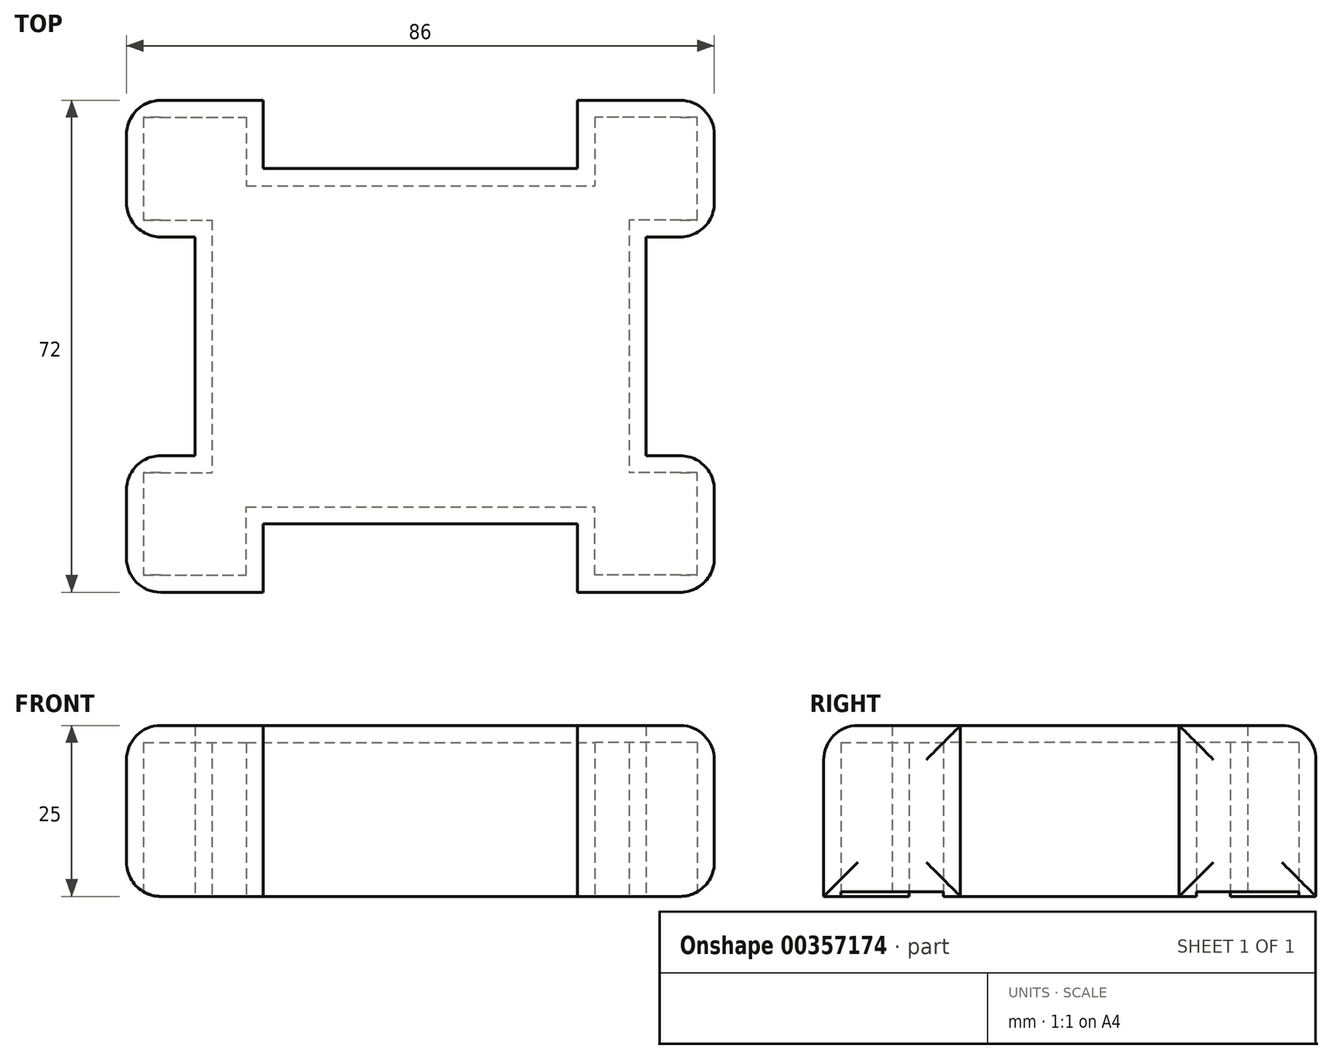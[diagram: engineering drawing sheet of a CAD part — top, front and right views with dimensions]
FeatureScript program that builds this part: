
annotation { "Feature Type Name" : "Feature", "Feature Type Description" : "" }
export const myFeature = defineFeature(function(context is Context, id is Id, definition is map)
    precondition{}
    {
        {
            var Q0;
            Q0=qCreatedBy(makeId("Top.planeOp"),FACE);
            var sketch = newSketch(context, id + "F0", { "sketchPlane" : qUnion([Q0])});
            skLineSegment(sketch, "E0.bottom", {"start": v(-33, 26) * mm, "end": v(33, 26) * mm});
            skLineSegment(sketch, "E0.top", {"start": v(-33, -26) * mm, "end": v(33, -26) * mm});
            skLineSegment(sketch, "E0.left", {"start": v(-33, 26) * mm, "end": v(-33, -26) * mm});
            skLineSegment(sketch, "E0.right", {"start": v(33, 26) * mm, "end": v(33, -26) * mm});
            skPoint(sketch, "E0.middle", {"position": v(0, 0) * mm});
            skLineSegment(sketch, "E1.bottom", {"start": v(-43, -36) * mm, "end": v(-23, -36) * mm});
            skLineSegment(sketch, "E1.top", {"start": v(-43, -16) * mm, "end": v(-23, -16) * mm});
            skLineSegment(sketch, "E1.left", {"start": v(-43, -36) * mm, "end": v(-43, -16) * mm});
            skLineSegment(sketch, "E1.right", {"start": v(-23, -36) * mm, "end": v(-23, -16) * mm});
            skPoint(sketch, "E1.middle", {"position": v(-33, -26) * mm});
            skLineSegment(sketch, "E2.bottom", {"start": v(43, -36) * mm, "end": v(23, -36) * mm});
            skLineSegment(sketch, "E2.top", {"start": v(43, -16) * mm, "end": v(23, -16) * mm});
            skLineSegment(sketch, "E2.left", {"start": v(43, -36) * mm, "end": v(43, -16) * mm});
            skLineSegment(sketch, "E2.right", {"start": v(23, -36) * mm, "end": v(23, -16) * mm});
            skPoint(sketch, "E2.middle", {"position": v(33, -26) * mm});
            skLineSegment(sketch, "E3.bottom", {"start": v(43, 36) * mm, "end": v(23, 36) * mm});
            skLineSegment(sketch, "E3.top", {"start": v(43, 16) * mm, "end": v(23, 16) * mm});
            skLineSegment(sketch, "E3.left", {"start": v(43, 36) * mm, "end": v(43, 16) * mm});
            skLineSegment(sketch, "E3.right", {"start": v(23, 36) * mm, "end": v(23, 16) * mm});
            skPoint(sketch, "E3.middle", {"position": v(33, 26) * mm});
            skLineSegment(sketch, "E4.bottom", {"start": v(-43, 36) * mm, "end": v(-23, 36) * mm});
            skLineSegment(sketch, "E4.top", {"start": v(-43, 16) * mm, "end": v(-23, 16) * mm});
            skLineSegment(sketch, "E4.left", {"start": v(-43, 36) * mm, "end": v(-43, 16) * mm});
            skLineSegment(sketch, "E4.right", {"start": v(-23, 36) * mm, "end": v(-23, 16) * mm});
            skPoint(sketch, "E4.middle", {"position": v(-33, 26) * mm});
            skSolve(sketch);
        }
        {
            var Q0;
            Q0 = qSketchRegion(id + "F0", true);
            extrude(context, id + "F1", {"entities" : qUnion([Q0]), "depth" : 25 * mm});
        }
        {
            var Q0;
            Q0=makeQuery(id+"F1.opExtrude","CAP_FACE",FACE,{"disambiguationData":[OSD([sQuery(id+"F0.wireOp",EDGE,"E0.bottom"),sQuery(id+"F0.wireOp",EDGE,"E0.top"),sQuery(id+"F0.wireOp",EDGE,"E0.left"),sQuery(id+"F0.wireOp",EDGE,"E0.right"),sQuery(id+"F0.wireOp",EDGE,"E1.bottom"),sQuery(id+"F0.wireOp",EDGE,"E1.top"),sQuery(id+"F0.wireOp",EDGE,"E1.left"),sQuery(id+"F0.wireOp",EDGE,"E1.right"),sQuery(id+"F0.wireOp",EDGE,"E2.bottom"),sQuery(id+"F0.wireOp",EDGE,"E2.top"),sQuery(id+"F0.wireOp",EDGE,"E2.left"),sQuery(id+"F0.wireOp",EDGE,"E2.right"),sQuery(id+"F0.wireOp",EDGE,"E3.bottom"),sQuery(id+"F0.wireOp",EDGE,"E3.top"),sQuery(id+"F0.wireOp",EDGE,"E3.left"),sQuery(id+"F0.wireOp",EDGE,"E3.right"),sQuery(id+"F0.wireOp",EDGE,"E4.bottom"),sQuery(id+"F0.wireOp",EDGE,"E4.top"),sQuery(id+"F0.wireOp",EDGE,"E4.left"),sQuery(id+"F0.wireOp",EDGE,"E4.right")])],"isStart":true});
            shell(context, id + "F2", {"entities" : qUnion([Q0]), "thickness" : 2.5 * mm});
        }
        {
            var Q0;
            Q0=makeQuery(id+"F1.opExtrude","CAP_EDGE",EDGE,{"disambiguationData":[OSD([sQuery(id+"F0.wireOp",EDGE,"E4.bottom")])],"isStart":false});
            var Q1;
            Q1=makeQuery(id+"F1.opExtrude","CAP_EDGE",EDGE,{"disambiguationData":[OSD([sQuery(id+"F0.wireOp",EDGE,"E1.bottom")])],"isStart":false});
            var Q2;
            Q2=makeQuery(id+"F1.opExtrude","CAP_EDGE",EDGE,{"disambiguationData":[OSD([sQuery(id+"F0.wireOp",EDGE,"E2.bottom")])],"isStart":false});
            var Q3;
            Q3=makeQuery(id+"F1.opExtrude","CAP_EDGE",EDGE,{"disambiguationData":[OSD([sQuery(id+"F0.wireOp",EDGE,"E3.bottom")])],"isStart":false});
            var Q4;
            Q4=makeQuery(id+"F1.opExtrude","CAP_EDGE",EDGE,{"disambiguationData":[OSD([sQuery(id+"F0.wireOp",EDGE,"E3.left")])],"isStart":false});
            var Q5;
            Q5=makeQuery(id+"F1.opExtrude","CAP_EDGE",EDGE,{"disambiguationData":[OSD([sQuery(id+"F0.wireOp",EDGE,"E2.left")])],"isStart":false});
            var Q6;
            Q6=makeQuery(id+"F1.opExtrude","CAP_EDGE",EDGE,{"disambiguationData":[OSD([sQuery(id+"F0.wireOp",EDGE,"E1.left")])],"isStart":false});
            var Q7;
            Q7=makeQuery(id+"F1.opExtrude","SWEPT_FACE",FACE,{"disambiguationData":[OSD([sQuery(id+"F0.wireOp",EDGE,"E4.left")])]});
            var Q8;
            Q8=makeQuery(id+"F1.opExtrude","SWEPT_FACE",FACE,{"disambiguationData":[OSD([sQuery(id+"F0.wireOp",EDGE,"E3.left")])]});
            var Q9;
            Q9=makeQuery(id+"F1.opExtrude","SWEPT_FACE",FACE,{"disambiguationData":[OSD([sQuery(id+"F0.wireOp",EDGE,"E2.left")])]});
            var Q10;
            Q10=makeQuery(id+"F1.opExtrude","SWEPT_FACE",FACE,{"disambiguationData":[OSD([sQuery(id+"F0.wireOp",EDGE,"E1.left")])]});
            fillet(context, id + "F3", {"entities" : qUnion([Q0, Q1, Q2, Q3, Q4, Q5, Q6, Q7, Q8, Q9, Q10]), "radius" : 5 * mm, "tangentPropagation" : true, "allowEdgeOverflow" : false});
        }
    });
